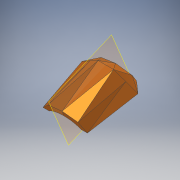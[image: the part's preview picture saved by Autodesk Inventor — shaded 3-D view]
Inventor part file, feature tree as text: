
AUTODESK INVENTOR PART (.ipt)
format: ipt  version: 2019 (Build 230136000, 136)  size: 172,544 bytes
history: native  units: mm
features: other x4, delete_face x1, direct_edit x1, plane x1
ambient origin geometry x8: Origin, YZ Plane, XZ Plane, XY Plane, X Axis, Y Axis, Z Axis, Center Point
bodies: Volumenkörper1 (feature_tree)
feature tree (7):
  other  "Main_afterRhino.ipt"
  delete_face  "Fläche löschen1"
  direct_edit  "Direktbearbeitung1"
  plane  "Arbeitsebene2"
  other  "Volumenkörper1::Main_afterRhino.ipt"
  other  "Bezeichnung1"
  other  "Skalierung1"
